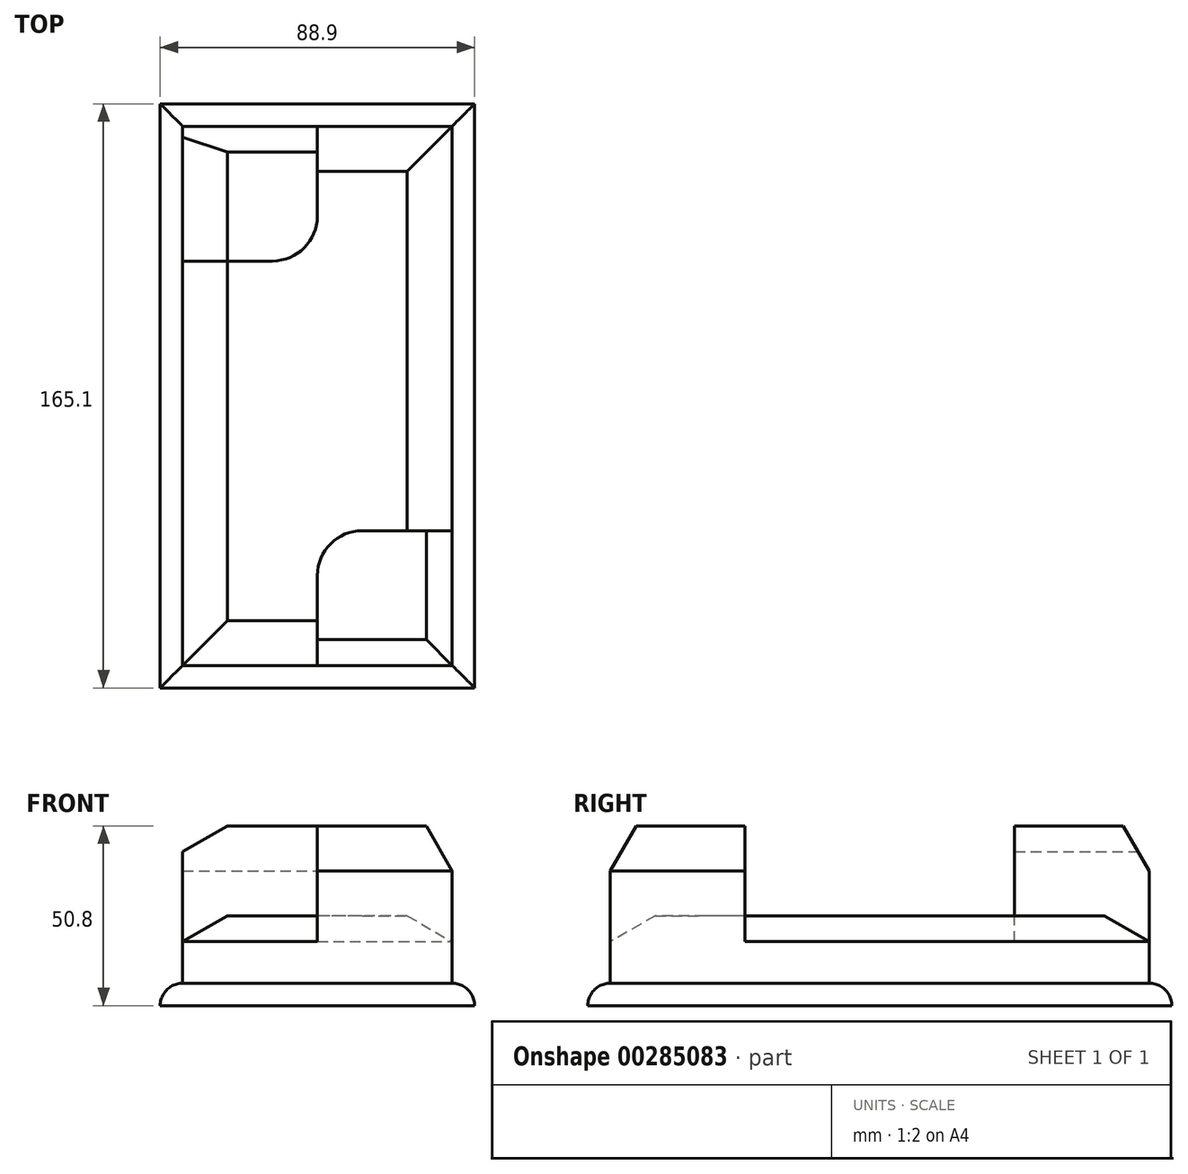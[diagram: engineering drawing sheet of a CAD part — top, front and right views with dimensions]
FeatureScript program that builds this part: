
annotation { "Feature Type Name" : "Feature", "Feature Type Description" : "" }
export const myFeature = defineFeature(function(context is Context, id is Id, definition is map)
    precondition{}
    {
        {
            var Q0;
            Q0=qCreatedBy(makeId("Top.planeOp"),FACE);
            var sketch = newSketch(context, id + "F0", { "sketchPlane" : qUnion([Q0])});
            skLineSegment(sketch, "E0.bottom", {"start": v(-96.16, 67.18) * mm, "end": v(-19.96, 67.18) * mm});
            skLineSegment(sketch, "E0.top", {"start": v(-96.16, -85.22) * mm, "end": v(-19.96, -85.22) * mm});
            skLineSegment(sketch, "E0.left", {"start": v(-96.16, 67.18) * mm, "end": v(-96.16, -85.22) * mm});
            skLineSegment(sketch, "E0.right", {"start": v(-19.96, 67.18) * mm, "end": v(-19.96, -85.22) * mm});
            skLineSegment(sketch, "E1.bottom", {"start": v(-102.5, 73.53) * mm, "end": v(-13.6, 73.53) * mm});
            skLineSegment(sketch, "E1.top", {"start": v(-102.5, -91.57) * mm, "end": v(-13.6, -91.57) * mm});
            skLineSegment(sketch, "E1.left", {"start": v(-102.5, 73.53) * mm, "end": v(-102.5, -91.57) * mm});
            skLineSegment(sketch, "E1.right", {"start": v(-13.6, 73.53) * mm, "end": v(-13.6, -91.57) * mm});
            skLineSegment(sketch, "E2", {"start": v(-96.16, 29.08) * mm, "end": v(-70.76, 29.08) * mm});
            skLineSegment(sketch, "E3", {"start": v(-58.06, 41.78) * mm, "end": v(-58.06, 67.18) * mm});
            skLineSegment(sketch, "E4", {"start": v(-58.06, -85.22) * mm, "end": v(-58.06, -59.82) * mm});
            skLineSegment(sketch, "E5", {"start": v(-45.36, -47.12) * mm, "end": v(-19.96, -47.12) * mm});
            skPoint(sketch, "E6.visualSharp", {"position": v(-58.06, 29.08) * mm});
            skArc(sketch, "E6.filletArc", {"start": v(-70.76, 29.08) * mm, "mid": v(-61.78, 32.8) * mm, "end": v(-58.06, 41.78) * mm});
            skPoint(sketch, "E7.visualSharp", {"position": v(-58.06, -47.12) * mm});
            skArc(sketch, "E7.filletArc", {"start": v(-45.36, -47.12) * mm, "mid": v(-54.34, -50.84) * mm, "end": v(-58.06, -59.82) * mm});
            skSolve(sketch);
        }
        {
            var Q0;
            {var subQ1=sQuery(id+"F0.wireOp",EDGE,"E4");Q0=makeQuery(id+"F0.imprint","IMPRINT",FACE,{"disambiguationData":[TD([[makeQuery(id+"F0.imprint","IMPRINT",EDGE,{"derivedFrom":subQ1}),-1.0]])]});}
            var Q1;
            {var subQ1=sQuery(id+"F0.wireOp",EDGE,"E2");Q1=makeQuery(id+"F0.imprint","IMPRINT",FACE,{"disambiguationData":[TD([[makeQuery(id+"F0.imprint","IMPRINT",EDGE,{"derivedFrom":subQ1}),1.0]])]});}
            extrude(context, id + "F1", {"entities" : qUnion([Q0, Q1]), "depth" : 50.8 * mm});
        }
        {
            var Q0;
            {var subQ3=sQuery(id+"F0.wireOp",EDGE,"E2");Q0=makeQuery(id+"F0.imprint","IMPRINT",FACE,{"disambiguationData":[TD([[makeQuery(id+"F0.imprint","IMPRINT",EDGE,{"derivedFrom":subQ3}),-1.0]])]});}
            extrude(context, id + "F2", {"entities" : qUnion([Q0]), "operationType" : NewBodyOperationType.ADD, "depth" : 25.4 * mm});
        }
        {
            var Q0;
            Q0=makeQuery(id+"F0.imprint","IMPRINT",FACE,{"disambiguationData":[TD([[makeQuery(id+"F0.imprint","IMPRINT",EDGE,{"derivedFrom":sQuery(id+"F0.wireOp",EDGE,"E1.bottom")}),-1.0]])]});
            extrude(context, id + "F3", {"entities" : qUnion([Q0]), "operationType" : NewBodyOperationType.ADD, "depth" : 6.35 * mm});
        }
        {
            var Q0;
            Q0=makeQuery(id+"F2.opExtrude","CAP_EDGE",EDGE,{"disambiguationData":[OSD([sQuery(id+"F0.wireOp",EDGE,"E0.left")])],"isStart":false});
            var Q1;
            Q1=makeQuery(id+"F2.opExtrude","CAP_EDGE",EDGE,{"disambiguationData":[OSD([sQuery(id+"F0.wireOp",EDGE,"E0.top")])],"isStart":false});
            var Q2;
            Q2=makeQuery(id+"F2.opExtrude","CAP_EDGE",EDGE,{"disambiguationData":[OSD([sQuery(id+"F0.wireOp",EDGE,"E0.right")])],"isStart":false});
            var Q3;
            Q3=makeQuery(id+"F2.opExtrude","CAP_EDGE",EDGE,{"disambiguationData":[OSD([sQuery(id+"F0.wireOp",EDGE,"E0.bottom")])],"isStart":false});
            chamfer(context, id + "F4", {"entities" : qUnion([Q0, Q1, Q2, Q3]), "chamferType" : ChamferType.OFFSET_ANGLE, "width" : 12.7 * mm, "oppositeDirection" : false, "angle" : 30 * degree, "tangentPropagation" : true});
        }
        {
            var Q0;
            Q0=makeQuery(id+"F1.opExtrude","CAP_EDGE",EDGE,{"disambiguationData":[OSD([sQuery(id+"F0.wireOp",EDGE,"E0.right")])],"isStart":false});
            var Q1;
            Q1=makeQuery(id+"F1.opExtrude","CAP_EDGE",EDGE,{"disambiguationData":[OSD([sQuery(id+"F0.wireOp",EDGE,"E0.top")])],"isStart":false});
            var Q2;
            Q2=makeQuery(id+"F1.opExtrude","CAP_EDGE",EDGE,{"disambiguationData":[OSD([sQuery(id+"F0.wireOp",EDGE,"E0.bottom")])],"isStart":false});
            var Q3;
            Q3=makeQuery(id+"F1.opExtrude","CAP_EDGE",EDGE,{"disambiguationData":[OSD([sQuery(id+"F0.wireOp",EDGE,"E0.left")])],"isStart":false});
            chamfer(context, id + "F5", {"entities" : qUnion([Q0, Q1, Q2, Q3]), "chamferType" : ChamferType.OFFSET_ANGLE, "width" : 12.7 * mm, "oppositeDirection" : false, "angle" : 30 * degree, "tangentPropagation" : true});
        }
        {
            var Q0;
            Q0=makeQuery(id+"F3.opExtrude","CAP_EDGE",EDGE,{"disambiguationData":[OSD([sQuery(id+"F0.wireOp",EDGE,"E1.top")])],"isStart":false});
            var Q1;
            Q1=makeQuery(id+"F3.opExtrude","CAP_EDGE",EDGE,{"disambiguationData":[OSD([sQuery(id+"F0.wireOp",EDGE,"E1.right")])],"isStart":false});
            var Q2;
            Q2=makeQuery(id+"F3.opExtrude","CAP_EDGE",EDGE,{"disambiguationData":[OSD([sQuery(id+"F0.wireOp",EDGE,"E1.left")])],"isStart":false});
            var Q3;
            Q3=makeQuery(id+"F3.opExtrude","CAP_EDGE",EDGE,{"disambiguationData":[OSD([sQuery(id+"F0.wireOp",EDGE,"E1.bottom")])],"isStart":false});
            fillet(context, id + "F6", {"entities" : qUnion([Q0, Q1, Q2, Q3]), "radius" : 6.35 * mm, "tangentPropagation" : true, "allowEdgeOverflow" : false});
        }
    });
